# Revit family: Electronics_Community_Biamp_Three-Way-Loudspeaker-System_R2-EN
name_source: partatom
category: Communication Devices
units: mm (PartAtom-declared; Revit-internal decimal feet)

## family parameters
Cut with Voids When Loaded = No
Host = Face
Maintain Annotation Orientation = No
OmniClass Number = 23.85.10.11.14.14.14
OmniClass Title = Loudspeakers
Part Type = Normal
Room Calculation Point = No
Round Connector Dimension = Use Diameter
Shared = No

## types (5) — shared parameters
Connector Description = Terminal strip; 200W continuous, 800W program 24.5 volts RMS, 49 volts momentary peak
Crossover Frequency = 600 Hz / 3.5 kHz
Default Elevation = 48 "
Depth = 31 "
Description = R2 High Output Full-Range 60°X 60° Weather-Resistant Loudspeaker
Driver Protection = DYNA-TECH protection circuitry
Drivers = LF 2 x 12 weather-treated, Ferrofluid-cooled MF 2 x M200 2 exit, non-metallic diaphragm,Ferrofluid-cooled HF 1 x 1 exit, titanium diaphragm
Enclosure = Hand-laminated fiberglass, light grey gelcoat
Environmental Performance = IEC529 IP55W rating with a minimum 5-degree downward aiming angle
Grill Material = Biamp - Plastic - Gray(Grid)
Grille = 3-layer WeatherStop™, light grey (Zinc-rich epoxy dual-layer powder coated perforated steel grille, foam, woven poly mesh)
Height = 25 "
Housing Material = Biamp - Plastic - Gray
Input Connection = 12 foot (4 m) SJOW #16 gauge
Loudspeaker Type = 3-way horn loaded triaxial, weather-resistant
Manufacturer = Biamp
Mounting/Rigging Provisions = (5) 1/2-13 rigging points
Optional Accessories = No optional accessories are available with products intended for EN54-24 installations
Product Documentation Link = https://downloads.biamp.com
Product Page URL = https://www.biamp.com
Product data url = https://bimobject.com
Required Accessories = 70 Hz high pass filter*, Equalization curve as specified on this spec sheet
Shipping Weight = 124.00 lb
Supplied Accessories = Weather-resistant mounting yoke, light grey
URL = https://www.biamp.com
Version = 1
Weight = 96.00 lb
Width = 25 "
Yoke Material = Biamp - Metal - Gray

## per-type parameters (varying)
| type | Broadband Sensitivity (1W/1m) | Broadband Sensitivity (1W/4m) | Maximum Average Output (1m) | Maximum Average Output (4m) | Maximum Peak Output (1m) | Minimum Impedance | Nominal Impedance | Operating Range | Rated Noise Power |
| R2-52Z-EN | 99.1 dB SPL (100Hz to 10 kHz 1/3 octave bands, EN54-24 frequency response requirements applied, EN54-24 impedance) | 87.1 dB SPL (100Hz to 10 kHz 1/3 octave bands, EN54-24 frequency response requirements applied, EN54-24 impedance) | 123.9 dB (EN54-24 frequency response requirements applied, 100 hr. rated noise power applied, EN54-24 Broadband Sensitivity) | 111.9 dB (EN54-24 frequency response requirements applied, 100 hr. rated noise power applied, EN54-24 Broadband Sensitivity) | 129.9 dB (EN54-24 frequency response requirements applied, 100 hr. rated noise power applied, EN54-24 Broadband Sensitivity, 6dB crest factor momentary peak) | 1.9 ohms @ 660 Hz | 2 ohms (to satisfy EN54-24 criteria) | 70 Hz to 16 kHz | 300W continuous, 24.5 volts RMS (EN54-24 100 hr. test, 6dB crest factor) |
| R2-77Z-EN | 99 dB SPL (100Hz to 10 kHz 1/3 octave bands, EN54-24 frequency response requirements applied, EN54-24 impedance) | 87 dB SPL (100Hz to 10 kHz 1/3 octave bands, EN54-24 frequency response requirements applied, EN54-24 impedance) | 122.1dB (EN54-24 frequency response requirements applied, 100 hr. rated noise power applied, EN54-24 Broadband Sensitivity) | 110.1dB (EN54-24 frequency response requirements applied, 100 hr. rated noise power applied, EN54-24 Broadband Sensitivity) | 128.1dB (EN54-24 frequency response requirements applied, 100 hr. rated noise power applied, EN54-24 Broadband Sensitivity, 6dB crest factor momentary peak) | 2.5 ohms @ 450 Hz | 3 ohms (to satisfy EN54-24 criteria) | 100 Hz to 10 kHz | 200W continuous, 24.5 volts RMS (EN54-24 100 hr. test, 6dB crest factor) |
| R2-94Z-EN | 98.3 dB SPL (100Hz to 10 kHz 1/3 octave bands, EN54-24 frequency response requirements applied, EN54-24 impedance) | 86.2 dB SPL (100Hz to 10 kHz 1/3 octave bands, EN54-24 frequency response requirements applied, EN54-24 impedance) | 121.3 dB (EN54-24 frequency response requirements applied, 100 hr. rated noise power applied, EN54-24 Broadband Sensitivity) | 109.3 dB (EN54-24 frequency response requirements applied, 100 hr. rated noise power applied, EN54-24 Broadband Sensitivity) | 127.3 dB (EN54-24 frequency response requirements applied, 100 hr. rated noise power applied, EN54-24 Broadband Sensitivity, 6dB crest factor momentary peak) | 2.4 ohms @ 450 Hz | 3 ohms (to satisfy EN54-24 criteria) | 100 Hz to 10 kHz | 200W continuous, 24.5 volts RMS (EN54-24 100 hr. test, 6dB crest factor) |
| R2-474Z-EN | 100.8 dB SPL (100Hz to 10 kHz 1/3 octave bands, EN54-24 frequency response requirements applied, EN54-24 impedance) | 88.7 dB SPL (100Hz to 10 kHz 1/3 octave bands, EN54-24 frequency response requirements applied, EN54-24 impedance) | 123.8 dB (EN54-24 frequency response requirements applied, 100 hr. rated noise power applied, EN54-24 Broadband Sensitivity) | 111.8 dB (EN54-24 frequency response requirements applied, 100 hr. rated noise power applied, EN54-24 Broadband Sensitivity) | 129.8 dB (EN54-24 frequency response requirements applied, 100 hr. rated noise power applied, EN54-24 Broadband Sensitivity, 6dB crest factor momentary peak) | 2.5 ohms @ 250 Hz | 3 ohms (to satisfy EN54-24 criteria) | 100 Hz to 10 kHz | 200W continuous, 24.5 volts RMS (EN54-24 100 hr. test, 6dB crest factor) |
| R2-694Z-EN | 99.8 dB SPL (100Hz to 10 kHz 1/3 octave bands, EN54-24 frequency response requirements applied, EN54-24 impedance) | 87.8 dB SPL (100Hz to 10 kHz 1/3 octave bands, EN54-24 frequency response requirements applied, EN54-24 impedance) | 122.8 dB (EN54-24 frequency response requirements applied, 100 hr. rated noise power applied, EN54-24 Broadband Sensitivity) | 110.9 dB (EN54-24 frequency response requirements applied, 100 hr. rated noise power applied, EN54-24 Broadband Sensitivity) | 128.8 dB (EN54-24 frequency response requirements applied, 100 hr. rated noise power applied, EN54-24 Broadband Sensitivity, 6dB crest factor momentary peak) | 2.5 ohms @ 480 Hz | 3 ohms (to satisfy EN54-24 criteria) | 100 Hz to 10 kHz | 200W continuous, 24.5 volts RMS (EN54-24 100 hr. test, 6dB crest factor) |

note: column(s) folded — value = type name in every type: Model

## geometry (parser evidence)
native form markers: Sweep x4
no freeform markers — native parametric forms only
